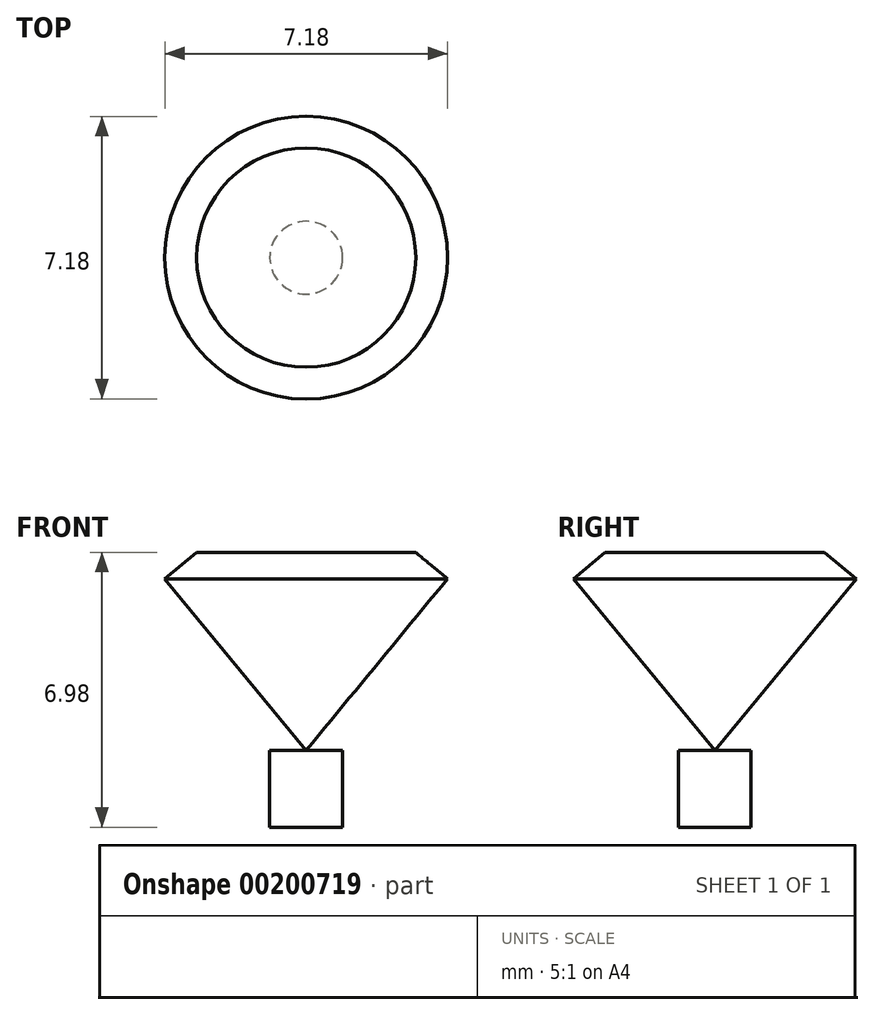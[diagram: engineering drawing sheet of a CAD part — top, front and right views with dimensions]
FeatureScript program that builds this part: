
annotation { "Feature Type Name" : "Feature", "Feature Type Description" : "" }
export const myFeature = defineFeature(function(context is Context, id is Id, definition is map)
    precondition{}
    {
        {
            var Q0;
            Q0=qCreatedBy(makeId("Top.planeOp"),FACE);
            var sketch = newSketch(context, id + "F0", { "sketchPlane" : qUnion([Q0])});
            skCircle(sketch, "E0", {"center": v(0, 0) * mm, "radius": 0.93 * mm});
            skSolve(sketch);
        }
        {
            var Q0;
            Q0=qSketchRegion(id+"F0",true);
            extrude(context, id + "F1", {"entities" : qUnion([Q0]), "depth" : 1.95 * mm});
        }
        {
            var Q0;
            Q0=qCreatedBy(makeId("Front.planeOp"),FACE);
            var sketch = newSketch(context, id + "F2", { "sketchPlane" : qUnion([Q0])});
            skPoint(sketch, "E1.0", {"position": v(0, 0) * mm});
            skLineSegment(sketch, "E2.0.0", {"start": v(-0.93, 1.95) * mm, "end": v(0.93, 1.95) * mm});
            skLineSegment(sketch, "E3", {"start": v(0, 1.95) * mm, "end": v(3.6, 6.31) * mm});
            skLineSegment(sketch, "E4", {"start": v(3.6, 6.31) * mm, "end": v(2.78, 6.98) * mm});
            skLineSegment(sketch, "E5", {"start": v(2.78, 6.98) * mm, "end": v(0, 6.98) * mm});
            skLineSegment(sketch, "E6", {"start": v(0, 6.98) * mm, "end": v(0, 1.95) * mm});
            skSolve(sketch);
        }
        {
            var Q0;
            Q0 = qSketchRegion(id + "F2", true);
            var Q1;
            Q1=sQuery(id+"F2.wireOp",EDGE,"E6");
            revolve(context, id + "F3", {"entities" : qUnion([Q0]), "axis" : qUnion([Q1]), "revolveType" : RevolveType.FULL});
        }
    });
